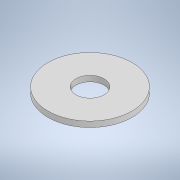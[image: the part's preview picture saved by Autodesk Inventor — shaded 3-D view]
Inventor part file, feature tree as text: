
AUTODESK INVENTOR PART (.ipt)
format: ipt  version: 2022 (Build 260153000, 153)  size: 99,840 bytes
history: native  units: in
note: dims shown in document units (in); Inventor stores cm internally (conversion verified against a paired STEP export)
features: extrude x2, sketch x2
ambient origin geometry x8: Origin, YZ Plane, XZ Plane, XY Plane, X Axis, Y Axis, Z Axis, Center Point
bodies: Solid1 (feature_tree)
feature tree (4):
  extrude  "Extrusion1"  Depth=0.0394in TaperAngle=0.0deg
  extrude  "Extrusion2"  Depth=0.0394in TaperAngle=0.0deg
  sketch  "Sketch1"  dims[d0=0.5906in d1=0.0394in d2=0.0in]
  sketch  "Sketch2"  dims[d3=0.1969in d4=0.0394in d5=0.0in]
